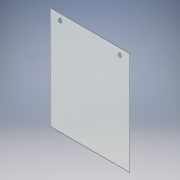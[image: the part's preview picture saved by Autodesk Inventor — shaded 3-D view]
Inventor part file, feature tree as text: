
AUTODESK INVENTOR PART (.ipt)
format: ipt  version: 2017 (Build 210142000, 142)  size: 105,472 bytes
history: native  units: in
note: dims shown in document units (in); Inventor stores cm internally (conversion verified against a paired STEP export)
features: extrude x1, sketch x1
ambient origin geometry x8: Origin, YZ Plane, XZ Plane, XY Plane, X Axis, Y Axis, Z Axis, Center Point
bodies: Body1 (feature_tree)
feature tree (2):
  extrude  "Extrusion2"  Depth=31.0in
  sketch  "Sketch1"  dims[d0=24.0in d1=31.0in d2=1.0in d5=2.0in d7=3.0in d11=0.5in d12=1.5in d13=0.093in d14=0.0in d17=1.5in d18=3.0in d19=2.0in]
